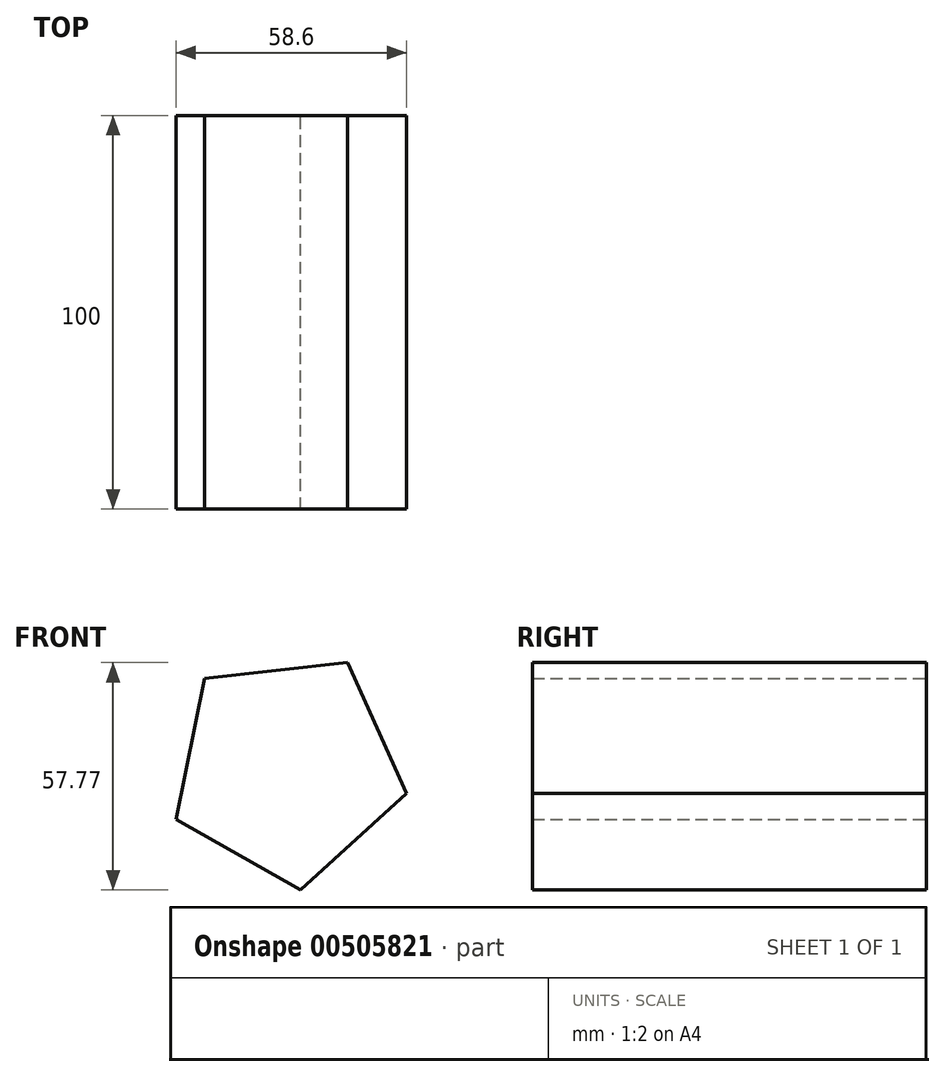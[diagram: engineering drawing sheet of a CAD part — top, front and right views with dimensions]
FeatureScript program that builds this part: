
annotation { "Feature Type Name" : "Feature", "Feature Type Description" : "" }
export const myFeature = defineFeature(function(context is Context, id is Id, definition is map)
    precondition{}
    {
        {
            var Q0;
            Q0=qCreatedBy(makeId("Front.planeOp"),FACE);
            var sketch = newSketch(context, id + "F0", { "sketchPlane" : qUnion([Q0])});
            skCircle(sketch, "E0.cCircle", {"center": v(0, 0) * mm, "radius": 25.08 * mm, "construction": true});
            skLineSegment(sketch, "E0.0", {"start": v(-28.23, -12.82) * mm, "end": v(-20.92, 22.89) * mm});
            skLineSegment(sketch, "E0.1", {"start": v(-20.92, 22.89) * mm, "end": v(15.3, 26.96) * mm});
            skLineSegment(sketch, "E0.2", {"start": v(15.3, 26.96) * mm, "end": v(30.37, -6.22) * mm});
            skLineSegment(sketch, "E0.3", {"start": v(30.37, -6.22) * mm, "end": v(3.47, -30.8) * mm});
            skLineSegment(sketch, "E0.4", {"start": v(3.47, -30.8) * mm, "end": v(-28.23, -12.82) * mm});
            skPoint(sketch, "E0.0.midPoint", {"position": v(-24.57, 5.03) * mm});
            skSolve(sketch);
        }
        {
            var Q0;
            Q0 = qSketchRegion(id + "F0", true);
            extrude(context, id + "F1", {"entities" : qUnion([Q0]), "endBound" : BoundingType.SYMMETRIC, "depth" : 100 * mm});
        }
    });
